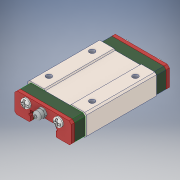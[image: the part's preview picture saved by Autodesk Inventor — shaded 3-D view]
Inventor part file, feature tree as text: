
AUTODESK INVENTOR PART (.ipt)
format: ipt  version: 2018 (Build 220112000, 112)  size: 883,712 bytes
history: native  units: in
note: dims shown in document units (in); Inventor stores cm internally (conversion verified against a paired STEP export)
features: chamfer x3, mirror x3, fillet x2, other x2
ambient origin geometry x8: Origin, YZ Plane, XZ Plane, XY Plane, X Axis, Y Axis, Z Axis, Center Point
bodies: Solid1 (feature_tree), Solid2 (feature_tree), Solid3 (feature_tree), Solid4 (feature_tree), Solid5 (feature_tree), Solid6 (feature_tree), Solid7 (feature_tree), Solid8 (feature_tree), Solid9 (feature_tree), Solid10 (feature_tree)
feature tree (10):
  chamfer  "Chamfer8"  [1 undecoded]
  chamfer  "Chamfer9"  [1 undecoded]
  chamfer  "Chamfer10"  [1 undecoded]
  fillet  "Fillet3"  [1 undecoded]
  mirror  "Mirror9"
  mirror  "Mirror10[1]"
  mirror  "Mirror10[2]"
  fillet  "Fillet5"  [1 undecoded]
  other  "Cut-Extrude9[1]"
  other  "Cut-Extrude9[2]"
note: 5 required parameter values undecoded (feature->parameter linkage not recoverable at this tier; creation-order binding heuristic only, values carry confidence <= 0.55)
